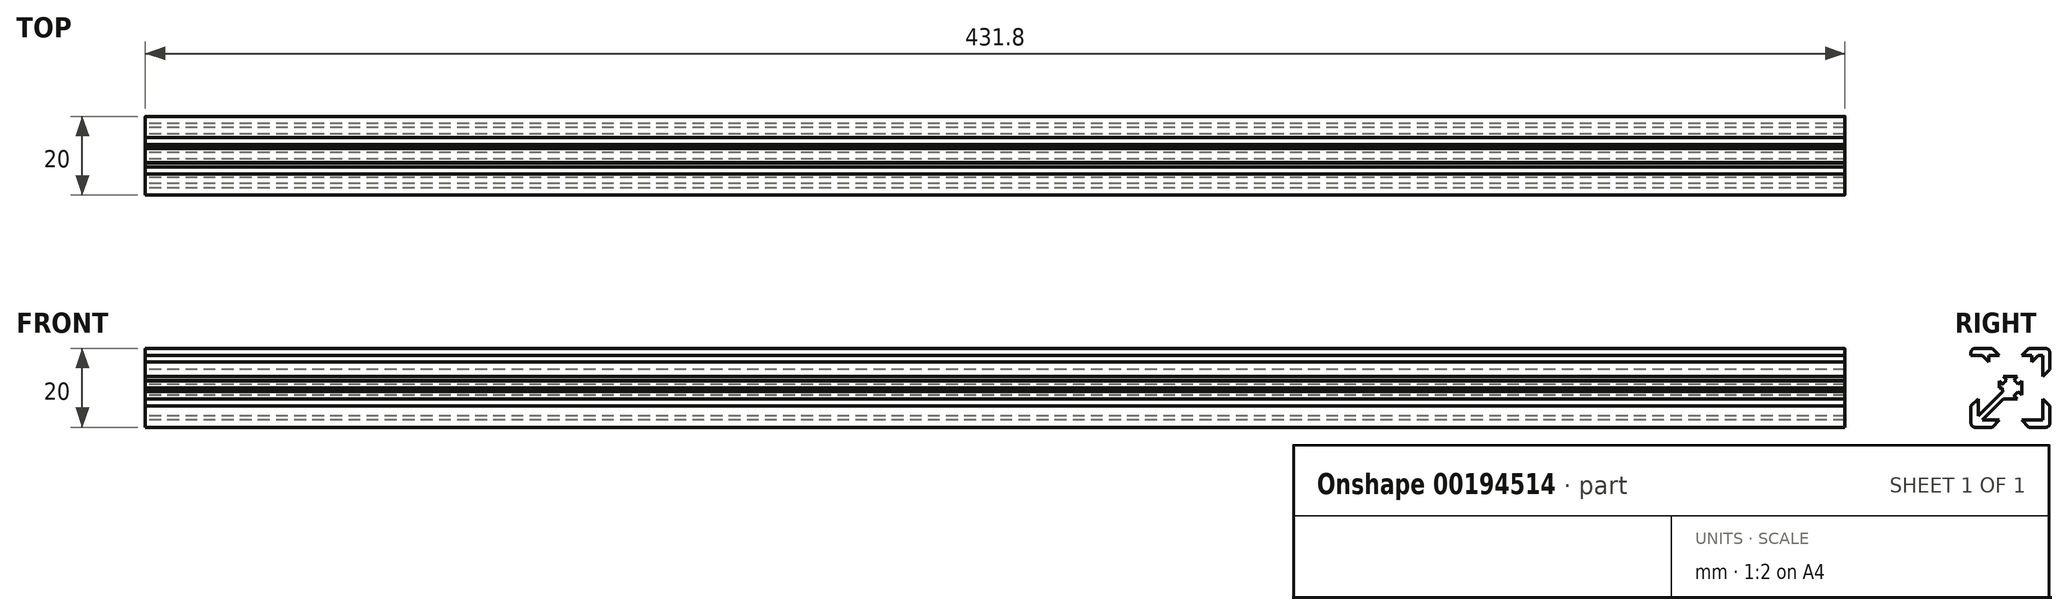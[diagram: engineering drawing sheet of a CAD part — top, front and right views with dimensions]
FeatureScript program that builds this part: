
annotation { "Feature Type Name" : "Feature", "Feature Type Description" : "" }
export const myFeature = defineFeature(function(context is Context, id is Id, definition is map)
    precondition{}
    {
        {
            var Q0;
            Q0=qCreatedBy(makeId("Right.planeOp"),FACE);
            var sketch = newSketch(context, id + "F0", { "sketchPlane" : qUnion([Q0])});
            skArc(sketch, "E0.filletArc", {"start": v(9, -10) * mm, "mid": v(9.7, -9.7) * mm, "end": v(10, -9) * mm});
            skArc(sketch, "E1", {"start": v(2.1, 0) * mm, "mid": v(1.48, -1.48) * mm, "end": v(0, -2.1) * mm});
            skLineSegment(sketch, "E2", {"start": v(0, -2.1) * mm, "end": v(0, -2.84) * mm});
            skLineSegment(sketch, "E3", {"start": v(2.1, 0) * mm, "end": v(2.84, 0) * mm});
            skLineSegment(sketch, "E4", {"start": v(2.84, -8.2) * mm, "end": v(4.64, -10) * mm});
            skLineSegment(sketch, "E5", {"start": v(8.2, -2.84) * mm, "end": v(10, -4.64) * mm});
            skLineSegment(sketch, "E6", {"start": v(4.64, -10) * mm, "end": v(9, -10) * mm});
            skLineSegment(sketch, "E7", {"start": v(10, -4.64) * mm, "end": v(10, -9) * mm});
            skLineSegment(sketch, "E8", {"start": v(2.84, -8.2) * mm, "end": v(10, -8.2) * mm});
            skLineSegment(sketch, "E9", {"start": v(8.2, -2.84) * mm, "end": v(8.2, -10) * mm});
            skLineSegment(sketch, "E10", {"start": v(9, -9) * mm, "end": v(8.2, -8.2) * mm});
            skPoint(sketch, "E11", {"position": v(8.73, -7.67) * mm});
            skPoint(sketch, "E12", {"position": v(7.67, -8.73) * mm});
            skPoint(sketch, "E13", {"position": v(8.2, -8.2) * mm});
            skPoint(sketch, "E14", {"position": v(5.53, -4.47) * mm});
            skPoint(sketch, "E15", {"position": v(4.47, -5.53) * mm});
            skLineSegment(sketch, "E16", {"start": v(7.67, -8.73) * mm, "end": v(4.47, -5.53) * mm});
            skLineSegment(sketch, "E17", {"start": v(8.73, -7.67) * mm, "end": v(5.53, -4.47) * mm});
            skLineSegment(sketch, "E18", {"start": v(5.53, -4.47) * mm, "end": v(1.92, -0.86) * mm});
            skLineSegment(sketch, "E19", {"start": v(4.47, -5.53) * mm, "end": v(0.86, -1.92) * mm});
            skLineSegment(sketch, "E20", {"start": v(8.2, -7.14) * mm, "end": v(8.2, -5.5) * mm});
            skLineSegment(sketch, "E21", {"start": v(7.14, -8.2) * mm, "end": v(5.5, -8.2) * mm});
            skLineSegment(sketch, "E22", {"start": v(5.5, -8.2) * mm, "end": v(5.5, -6.56) * mm});
            skLineSegment(sketch, "E23", {"start": v(8.2, -5.5) * mm, "end": v(6.56, -5.5) * mm});
            skLineSegment(sketch, "E24", {"start": v(2.84, 0) * mm, "end": v(2.84, -1.78) * mm});
            skLineSegment(sketch, "E25", {"start": v(0, -2.84) * mm, "end": v(1.78, -2.84) * mm});
            skArc(sketch, "E26.filletArc", {"start": v(10, 9) * mm, "mid": v(9.7, 9.7) * mm, "end": v(9, 10) * mm});
            skArc(sketch, "E27", {"start": v(0, 2.1) * mm, "mid": v(1.48, 1.48) * mm, "end": v(2.1, 0) * mm});
            skLineSegment(sketch, "E28", {"start": v(0, 2.1) * mm, "end": v(0, 2.84) * mm});
            skLineSegment(sketch, "E29", {"start": v(8.2, 2.84) * mm, "end": v(10, 4.64) * mm});
            skLineSegment(sketch, "E30", {"start": v(2.84, 8.2) * mm, "end": v(4.64, 10) * mm});
            skLineSegment(sketch, "E31", {"start": v(10, 4.64) * mm, "end": v(10, 9) * mm});
            skLineSegment(sketch, "E32", {"start": v(4.64, 10) * mm, "end": v(9, 10) * mm});
            skLineSegment(sketch, "E33", {"start": v(8.2, 2.84) * mm, "end": v(8.2, 10) * mm});
            skLineSegment(sketch, "E34", {"start": v(2.84, 8.2) * mm, "end": v(10, 8.2) * mm});
            skLineSegment(sketch, "E35", {"start": v(9, 9) * mm, "end": v(8.2, 8.2) * mm});
            skPoint(sketch, "E36", {"position": v(7.67, 8.73) * mm});
            skPoint(sketch, "E37", {"position": v(8.73, 7.67) * mm});
            skPoint(sketch, "E38", {"position": v(8.2, 8.2) * mm});
            skPoint(sketch, "E39", {"position": v(4.47, 5.53) * mm});
            skPoint(sketch, "E40", {"position": v(5.53, 4.47) * mm});
            skLineSegment(sketch, "E41", {"start": v(8.73, 7.67) * mm, "end": v(5.53, 4.47) * mm});
            skLineSegment(sketch, "E42", {"start": v(7.67, 8.73) * mm, "end": v(4.47, 5.53) * mm});
            skLineSegment(sketch, "E43", {"start": v(4.47, 5.53) * mm, "end": v(0.86, 1.92) * mm});
            skLineSegment(sketch, "E44", {"start": v(5.53, 4.47) * mm, "end": v(1.92, 0.86) * mm});
            skLineSegment(sketch, "E45", {"start": v(7.14, 8.2) * mm, "end": v(5.5, 8.2) * mm});
            skLineSegment(sketch, "E46", {"start": v(8.2, 7.14) * mm, "end": v(8.2, 5.5) * mm});
            skLineSegment(sketch, "E47", {"start": v(8.2, 5.5) * mm, "end": v(6.56, 5.5) * mm});
            skLineSegment(sketch, "E48", {"start": v(5.5, 8.2) * mm, "end": v(5.5, 6.56) * mm});
            skLineSegment(sketch, "E49", {"start": v(0, 2.84) * mm, "end": v(1.78, 2.84) * mm});
            skLineSegment(sketch, "E50", {"start": v(2.84, 0) * mm, "end": v(2.84, 1.78) * mm});
            skArc(sketch, "E51.filletArc", {"start": v(-9, 10) * mm, "mid": v(-9.7, 9.7) * mm, "end": v(-10, 9) * mm});
            skArc(sketch, "E52", {"start": v(-2.1, 0) * mm, "mid": v(-1.48, 1.48) * mm, "end": v(0, 2.1) * mm});
            skLineSegment(sketch, "E53", {"start": v(-2.1, 0) * mm, "end": v(-2.84, 0) * mm});
            skLineSegment(sketch, "E54", {"start": v(-2.84, 8.2) * mm, "end": v(-4.64, 10) * mm});
            skLineSegment(sketch, "E55", {"start": v(-8.2, 2.84) * mm, "end": v(-10, 4.64) * mm});
            skLineSegment(sketch, "E56", {"start": v(-4.64, 10) * mm, "end": v(-9, 10) * mm});
            skLineSegment(sketch, "E57", {"start": v(-10, 4.64) * mm, "end": v(-10, 9) * mm});
            skLineSegment(sketch, "E58", {"start": v(-2.84, 8.2) * mm, "end": v(-10, 8.2) * mm});
            skLineSegment(sketch, "E59", {"start": v(-8.2, 2.84) * mm, "end": v(-8.2, 10) * mm});
            skLineSegment(sketch, "E60", {"start": v(-9, 9) * mm, "end": v(-8.2, 8.2) * mm});
            skPoint(sketch, "E61", {"position": v(-8.73, 7.67) * mm});
            skPoint(sketch, "E62", {"position": v(-7.67, 8.73) * mm});
            skPoint(sketch, "E63", {"position": v(-8.2, 8.2) * mm});
            skPoint(sketch, "E64", {"position": v(-5.53, 4.47) * mm});
            skPoint(sketch, "E65", {"position": v(-4.47, 5.53) * mm});
            skLineSegment(sketch, "E66", {"start": v(-7.67, 8.73) * mm, "end": v(-4.47, 5.53) * mm});
            skLineSegment(sketch, "E67", {"start": v(-8.73, 7.67) * mm, "end": v(-5.53, 4.47) * mm});
            skLineSegment(sketch, "E68", {"start": v(-5.53, 4.47) * mm, "end": v(-1.92, 0.86) * mm});
            skLineSegment(sketch, "E69", {"start": v(-4.47, 5.53) * mm, "end": v(-0.86, 1.92) * mm});
            skLineSegment(sketch, "E70", {"start": v(-8.2, 7.14) * mm, "end": v(-8.2, 5.5) * mm});
            skLineSegment(sketch, "E71", {"start": v(-7.14, 8.2) * mm, "end": v(-5.5, 8.2) * mm});
            skLineSegment(sketch, "E72", {"start": v(-5.5, 8.2) * mm, "end": v(-5.5, 6.56) * mm});
            skLineSegment(sketch, "E73", {"start": v(-8.2, 5.5) * mm, "end": v(-6.56, 5.5) * mm});
            skLineSegment(sketch, "E74", {"start": v(-2.84, 0) * mm, "end": v(-2.84, 1.78) * mm});
            skLineSegment(sketch, "E75", {"start": v(0, 2.84) * mm, "end": v(-1.78, 2.84) * mm});
            skArc(sketch, "E76.filletArc", {"start": v(-10, -9) * mm, "mid": v(-9.7, -9.7) * mm, "end": v(-9, -10) * mm});
            skArc(sketch, "E77", {"start": v(0, -2.1) * mm, "mid": v(-1.48, -1.48) * mm, "end": v(-2.1, 0) * mm});
            skLineSegment(sketch, "E78", {"start": v(-8.2, -2.84) * mm, "end": v(-10, -4.64) * mm});
            skLineSegment(sketch, "E79", {"start": v(-2.84, -8.2) * mm, "end": v(-4.64, -10) * mm});
            skLineSegment(sketch, "E80", {"start": v(-10, -4.64) * mm, "end": v(-10, -9) * mm});
            skLineSegment(sketch, "E81", {"start": v(-4.64, -10) * mm, "end": v(-9, -10) * mm});
            skLineSegment(sketch, "E82", {"start": v(-8.2, -2.84) * mm, "end": v(-8.2, -10) * mm});
            skLineSegment(sketch, "E83", {"start": v(-2.84, -8.2) * mm, "end": v(-10, -8.2) * mm});
            skLineSegment(sketch, "E84", {"start": v(-9, -9) * mm, "end": v(-8.2, -8.2) * mm});
            skPoint(sketch, "E85", {"position": v(-7.67, -8.73) * mm});
            skPoint(sketch, "E86", {"position": v(-8.73, -7.67) * mm});
            skPoint(sketch, "E87", {"position": v(-8.2, -8.2) * mm});
            skPoint(sketch, "E88", {"position": v(-4.47, -5.53) * mm});
            skPoint(sketch, "E89", {"position": v(-5.53, -4.47) * mm});
            skLineSegment(sketch, "E90", {"start": v(-8.73, -7.67) * mm, "end": v(-5.53, -4.47) * mm});
            skLineSegment(sketch, "E91", {"start": v(-7.67, -8.73) * mm, "end": v(-4.47, -5.53) * mm});
            skLineSegment(sketch, "E92", {"start": v(-4.47, -5.53) * mm, "end": v(-0.86, -1.92) * mm});
            skLineSegment(sketch, "E93", {"start": v(-5.53, -4.47) * mm, "end": v(-1.92, -0.86) * mm});
            skLineSegment(sketch, "E94", {"start": v(-7.14, -8.2) * mm, "end": v(-5.5, -8.2) * mm});
            skLineSegment(sketch, "E95", {"start": v(-8.2, -7.14) * mm, "end": v(-8.2, -5.5) * mm});
            skLineSegment(sketch, "E96", {"start": v(-8.2, -5.5) * mm, "end": v(-6.56, -5.5) * mm});
            skLineSegment(sketch, "E97", {"start": v(-5.5, -8.2) * mm, "end": v(-5.5, -6.56) * mm});
            skLineSegment(sketch, "E98", {"start": v(0, -2.84) * mm, "end": v(-1.78, -2.84) * mm});
            skLineSegment(sketch, "E99", {"start": v(-2.84, 0) * mm, "end": v(-2.84, -1.78) * mm});
            skLineSegment(sketch, "E100", {"start": v(-1.78, -2.84) * mm, "end": v(-2.84, -1.78) * mm});
            skLineSegment(sketch, "E101", {"start": v(-10, 8.2) * mm, "end": v(-10, 9) * mm});
            skLineSegment(sketch, "E102", {"start": v(-9, 10) * mm, "end": v(-4.64, 10) * mm});
            skLineSegment(sketch, "E103", {"start": v(-2.84, 8.2) * mm, "end": v(-7.14, 8.2) * mm});
            skLineSegment(sketch, "E104", {"start": v(-1.78, 2.84) * mm, "end": v(1.78, 2.84) * mm});
            skLineSegment(sketch, "E105", {"start": v(7.14, 8.2) * mm, "end": v(2.84, 8.2) * mm});
            skLineSegment(sketch, "E106", {"start": v(10, 9) * mm, "end": v(10, 4.64) * mm});
            skLineSegment(sketch, "E107", {"start": v(8.2, 2.84) * mm, "end": v(8.2, 5.5) * mm});
            skSolve(sketch);
        }
        {
            var Q0;
            {var subQ5=sQuery(id+"F0.wireOp",EDGE,"E0.filletArc");Q0=makeQuery(id+"F0.imprint","IMPRINT",FACE,{"disambiguationData":[TD([[makeQuery(id+"F0.imprint","IMPRINT",EDGE,{"derivedFrom":subQ5}),1.0]])]});}
            var Q1;
            {var subQ0=sQuery(id+"F0.wireOp",EDGE,"E21");Q1=makeQuery(id+"F0.imprint","IMPRINT",FACE,{"disambiguationData":[TD([[makeQuery(id+"F0.imprint","IMPRINT",EDGE,{"derivedFrom":subQ0}),-1.0]])]});}
            var Q2;
            {var subQ0=sQuery(id+"F0.wireOp",EDGE,"E20");Q2=makeQuery(id+"F0.imprint","IMPRINT",FACE,{"disambiguationData":[TD([[makeQuery(id+"F0.imprint","IMPRINT",EDGE,{"derivedFrom":subQ0}),1.0]])]});}
            var Q3;
            {var subQ6=sQuery(id+"F0.wireOp",EDGE,"E26.filletArc");Q3=makeQuery(id+"F0.imprint","IMPRINT",FACE,{"disambiguationData":[TD([[makeQuery(id+"F0.imprint","IMPRINT",EDGE,{"derivedFrom":subQ6}),1.0]])]});}
            var Q4;
            {var subQ0=sQuery(id+"F0.wireOp",EDGE,"E46");Q4=makeQuery(id+"F0.imprint","IMPRINT",FACE,{"disambiguationData":[TD([[makeQuery(id+"F0.imprint","IMPRINT",EDGE,{"derivedFrom":subQ0}),-1.0]])]});}
            var Q5;
            {var subQ3=sQuery(id+"F0.wireOp",EDGE,"E48");Q5=makeQuery(id+"F0.imprint","IMPRINT",FACE,{"disambiguationData":[TD([[makeQuery(id+"F0.imprint","IMPRINT",EDGE,{"derivedFrom":subQ3}),1.0]])]});}
            var Q6;
            {var subQ6=sQuery(id+"F0.wireOp",EDGE,"E51.filletArc");Q6=makeQuery(id+"F0.imprint","IMPRINT",FACE,{"disambiguationData":[TD([[makeQuery(id+"F0.imprint","IMPRINT",EDGE,{"derivedFrom":subQ6}),1.0]])]});}
            var Q7;
            {var subQ3=sQuery(id+"F0.wireOp",EDGE,"E72");Q7=makeQuery(id+"F0.imprint","IMPRINT",FACE,{"disambiguationData":[TD([[makeQuery(id+"F0.imprint","IMPRINT",EDGE,{"derivedFrom":subQ3}),-1.0]])]});}
            var Q8;
            {var subQ0=sQuery(id+"F0.wireOp",EDGE,"E70");Q8=makeQuery(id+"F0.imprint","IMPRINT",FACE,{"disambiguationData":[TD([[makeQuery(id+"F0.imprint","IMPRINT",EDGE,{"derivedFrom":subQ0}),1.0]])]});}
            var Q9;
            {var subQ5=sQuery(id+"F0.wireOp",EDGE,"E76.filletArc");Q9=makeQuery(id+"F0.imprint","IMPRINT",FACE,{"disambiguationData":[TD([[makeQuery(id+"F0.imprint","IMPRINT",EDGE,{"derivedFrom":subQ5}),1.0]])]});}
            var Q10;
            {var subQ0=sQuery(id+"F0.wireOp",EDGE,"E95");Q10=makeQuery(id+"F0.imprint","IMPRINT",FACE,{"disambiguationData":[TD([[makeQuery(id+"F0.imprint","IMPRINT",EDGE,{"derivedFrom":subQ0}),-1.0]])]});}
            var Q11;
            {var subQ0=sQuery(id+"F0.wireOp",EDGE,"E94");Q11=makeQuery(id+"F0.imprint","IMPRINT",FACE,{"disambiguationData":[TD([[makeQuery(id+"F0.imprint","IMPRINT",EDGE,{"derivedFrom":subQ0}),1.0]])]});}
            var Q12;
            {var subQ4=sQuery(id+"F0.wireOp",EDGE,"E24");Q12=makeQuery(id+"F0.imprint","IMPRINT",FACE,{"disambiguationData":[TD([[makeQuery(id+"F0.imprint","IMPRINT",EDGE,{"derivedFrom":subQ4}),-1.0]])]});}
            var Q13;
            {var subQ4=sQuery(id+"F0.wireOp",EDGE,"E25");Q13=makeQuery(id+"F0.imprint","IMPRINT",FACE,{"disambiguationData":[TD([[makeQuery(id+"F0.imprint","IMPRINT",EDGE,{"derivedFrom":subQ4}),1.0]])]});}
            var Q14;
            {var subQ0=sQuery(id+"F0.wireOp",EDGE,"E2");Q14=makeQuery(id+"F0.imprint","IMPRINT",FACE,{"disambiguationData":[TD([[makeQuery(id+"F0.imprint","IMPRINT",EDGE,{"derivedFrom":subQ0}),1.0]])]});}
            var Q15;
            {var subQ0=sQuery(id+"F0.wireOp",EDGE,"E2");Q15=makeQuery(id+"F0.imprint","IMPRINT",FACE,{"disambiguationData":[TD([[makeQuery(id+"F0.imprint","IMPRINT",EDGE,{"derivedFrom":subQ0}),-1.0]])]});}
            var Q16;
            {var subQ4=sQuery(id+"F0.wireOp",EDGE,"E4");Q16=makeQuery(id+"F0.imprint","IMPRINT",FACE,{"disambiguationData":[TD([[makeQuery(id+"F0.imprint","IMPRINT",EDGE,{"derivedFrom":subQ4}),1.0]])]});}
            var Q17;
            {var subQ1=sQuery(id+"F0.wireOp",EDGE,"E5");Q17=makeQuery(id+"F0.imprint","IMPRINT",FACE,{"disambiguationData":[TD([[makeQuery(id+"F0.imprint","IMPRINT",EDGE,{"derivedFrom":subQ1}),-1.0]])]});}
            var Q18;
            {var subQ0=sQuery(id+"F0.wireOp",EDGE,"E28");Q18=makeQuery(id+"F0.imprint","IMPRINT",FACE,{"disambiguationData":[TD([[makeQuery(id+"F0.imprint","IMPRINT",EDGE,{"derivedFrom":subQ0}),-1.0]])]});}
            var Q19;
            {var subQ0=sQuery(id+"F0.wireOp",EDGE,"E3");Q19=makeQuery(id+"F0.imprint","IMPRINT",FACE,{"disambiguationData":[TD([[makeQuery(id+"F0.imprint","IMPRINT",EDGE,{"derivedFrom":subQ0}),1.0]])]});}
            var Q20;
            {var subQ0=sQuery(id+"F0.wireOp",EDGE,"E28");Q20=makeQuery(id+"F0.imprint","IMPRINT",FACE,{"disambiguationData":[TD([[makeQuery(id+"F0.imprint","IMPRINT",EDGE,{"derivedFrom":subQ0}),1.0]])]});}
            var Q21;
            {var subQ0=sQuery(id+"F0.wireOp",EDGE,"E28");Q21=makeQuery(id+"F0.imprint","IMPRINT",FACE,{"disambiguationData":[TD([[makeQuery(id+"F0.imprint","IMPRINT",EDGE,{"derivedFrom":subQ0}),-1.0]])]});}
            var Q22;
            {var subQ5=sQuery(id+"F0.wireOp",EDGE,"E29");Q22=makeQuery(id+"F0.imprint","IMPRINT",FACE,{"disambiguationData":[TD([[makeQuery(id+"F0.imprint","IMPRINT",EDGE,{"derivedFrom":subQ5}),1.0]])]});}
            var Q23;
            {var subQ4=sQuery(id+"F0.wireOp",EDGE,"E30");Q23=makeQuery(id+"F0.imprint","IMPRINT",FACE,{"disambiguationData":[TD([[makeQuery(id+"F0.imprint","IMPRINT",EDGE,{"derivedFrom":subQ4}),-1.0]])]});}
            var Q24;
            {var subQ4=sQuery(id+"F0.wireOp",EDGE,"E74");Q24=makeQuery(id+"F0.imprint","IMPRINT",FACE,{"disambiguationData":[TD([[makeQuery(id+"F0.imprint","IMPRINT",EDGE,{"derivedFrom":subQ4}),-1.0]])]});}
            var Q25;
            {var subQ1=sQuery(id+"F0.wireOp",EDGE,"E54");Q25=makeQuery(id+"F0.imprint","IMPRINT",FACE,{"disambiguationData":[TD([[makeQuery(id+"F0.imprint","IMPRINT",EDGE,{"derivedFrom":subQ1}),1.0]])]});}
            var Q26;
            {var subQ5=sQuery(id+"F0.wireOp",EDGE,"E57");Q26=makeQuery(id+"F0.imprint","IMPRINT",FACE,{"disambiguationData":[TD([[makeQuery(id+"F0.imprint","IMPRINT",EDGE,{"derivedFrom":subQ5}),-1.0]])]});}
            var Q27;
            {var subQ0=sQuery(id+"F0.wireOp",EDGE,"E53");Q27=makeQuery(id+"F0.imprint","IMPRINT",FACE,{"disambiguationData":[TD([[makeQuery(id+"F0.imprint","IMPRINT",EDGE,{"derivedFrom":subQ0}),1.0]])]});}
            var Q28;
            {var subQ4=sQuery(id+"F0.wireOp",EDGE,"E78");Q28=makeQuery(id+"F0.imprint","IMPRINT",FACE,{"disambiguationData":[TD([[makeQuery(id+"F0.imprint","IMPRINT",EDGE,{"derivedFrom":subQ4}),1.0]])]});}
            var Q29;
            {var subQ1=sQuery(id+"F0.wireOp",EDGE,"E79");Q29=makeQuery(id+"F0.imprint","IMPRINT",FACE,{"disambiguationData":[TD([[makeQuery(id+"F0.imprint","IMPRINT",EDGE,{"derivedFrom":subQ1}),-1.0]])]});}
            var Q30;
            {var subQ5=sQuery(id+"F0.wireOp",EDGE,"E100");Q30=makeQuery(id+"F0.imprint","IMPRINT",FACE,{"disambiguationData":[TD([[makeQuery(id+"F0.imprint","IMPRINT",EDGE,{"derivedFrom":subQ5}),-1.0]])]});}
            var Q31;
            {var subQ6=sQuery(id+"F0.wireOp",EDGE,"E100");Q31=makeQuery(id+"F0.imprint","IMPRINT",FACE,{"disambiguationData":[TD([[makeQuery(id+"F0.imprint","IMPRINT",EDGE,{"derivedFrom":subQ6}),1.0]])]});}
            var Q32;
            {var subQ0=sQuery(id+"F0.wireOp",EDGE,"E18");var subQ15=sQuery(id+"F0.wireOp",EDGE,"E1");var subQ16=makeQuery(id+"F0.imprint","INTERSECT",VERTEX,{"derivedFrom":[subQ15,subQ0]});Q32=makeQuery(id+"F0.imprint","IMPRINT",FACE,{"disambiguationData":[TD([[makeQuery(id+"F0.imprint","IMPRINT",EDGE,{"disambiguationData":[TD([[subQ16,-1.0]])],"derivedFrom":subQ15}),1.0]])]});}
            var Q33;
            {var subQ4=sQuery(id+"F0.wireOp",EDGE,"E43");var subQ5=sQuery(id+"F0.wireOp",EDGE,"E27");var subQ6=makeQuery(id+"F0.imprint","INTERSECT",VERTEX,{"derivedFrom":[subQ5,subQ4]});Q33=makeQuery(id+"F0.imprint","IMPRINT",FACE,{"disambiguationData":[TD([[makeQuery(id+"F0.imprint","IMPRINT",EDGE,{"disambiguationData":[TD([[subQ6,-1.0]])],"derivedFrom":subQ5}),1.0]])]});}
            var Q34;
            {var subQ0=sQuery(id+"F0.wireOp",EDGE,"E68");var subQ9=sQuery(id+"F0.wireOp",EDGE,"E52");var subQ10=makeQuery(id+"F0.imprint","INTERSECT",VERTEX,{"derivedFrom":[subQ9,subQ0]});Q34=makeQuery(id+"F0.imprint","IMPRINT",FACE,{"disambiguationData":[TD([[makeQuery(id+"F0.imprint","IMPRINT",EDGE,{"disambiguationData":[TD([[subQ10,-1.0]])],"derivedFrom":subQ9}),1.0]])]});}
            var Q35;
            Q35=sQuery(id+"F0.wireOp",EDGE,"E1");
            var Q36;
            Q36=sQuery(id+"F0.wireOp",EDGE,"E77");
            var Q37;
            Q37=sQuery(id+"F0.wireOp",EDGE,"E52");
            var Q38;
            Q38=sQuery(id+"F0.wireOp",EDGE,"E27");
            var Q39;
            Q39=sQuery(id+"F0.wireOp",EDGE,"E44");
            var Q40;
            Q40=sQuery(id+"F0.wireOp",EDGE,"E41");
            var Q41;
            Q41=sQuery(id+"F0.wireOp",EDGE,"E47");
            var Q42;
            Q42=sQuery(id+"F0.wireOp",EDGE,"E107");
            var Q43;
            Q43=sQuery(id+"F0.wireOp",EDGE,"E29");
            var Q44;
            Q44=sQuery(id+"F0.wireOp",EDGE,"E106");
            var Q45;
            Q45=sQuery(id+"F0.wireOp",EDGE,"E26.filletArc");
            var Q46;
            Q46=sQuery(id+"F0.wireOp",EDGE,"E32");
            var Q47;
            Q47=sQuery(id+"F0.wireOp",EDGE,"E30");
            var Q48;
            Q48=sQuery(id+"F0.wireOp",EDGE,"E34");
            var Q49;
            Q49=sQuery(id+"F0.wireOp",EDGE,"E48");
            var Q50;
            Q50=sQuery(id+"F0.wireOp",EDGE,"E42");
            var Q51;
            Q51=sQuery(id+"F0.wireOp",EDGE,"E43");
            var Q52;
            Q52=sQuery(id+"F0.wireOp",EDGE,"E104");
            var Q53;
            Q53=sQuery(id+"F0.wireOp",EDGE,"E69");
            var Q54;
            Q54=sQuery(id+"F0.wireOp",EDGE,"E66");
            var Q55;
            Q55=sQuery(id+"F0.wireOp",EDGE,"E72");
            var Q56;
            Q56=sQuery(id+"F0.wireOp",EDGE,"E58");
            var Q57;
            Q57=sQuery(id+"F0.wireOp",EDGE,"E54");
            var Q58;
            Q58=sQuery(id+"F0.wireOp",EDGE,"E56");
            var Q59;
            Q59=sQuery(id+"F0.wireOp",EDGE,"E51.filletArc");
            var Q60;
            Q60=sQuery(id+"F0.wireOp",EDGE,"E57");
            var Q61;
            Q61=sQuery(id+"F0.wireOp",EDGE,"E55");
            extrude(context, id + "F1", {"entities" : qUnion([Q0, Q1, Q2, Q3, Q4, Q5, Q6, Q7, Q8, Q9, Q10, Q11, Q12, Q13, Q14, Q15, Q16, Q17, Q18, Q19, Q20, Q21, Q22, Q23, Q24, Q25, Q26, Q27, Q28, Q29, Q30, Q31, Q32, Q33, Q34]), "surfaceEntities" : qUnion([Q35, Q36, Q37, Q38, Q39, Q40, Q41, Q42, Q43, Q44, Q45, Q46, Q47, Q48, Q49, Q50, Q51, Q52, Q53, Q54, Q55, Q56, Q57, Q58, Q59, Q60, Q61]), "depth" : 431.8 * mm, "offsetDistance" : 25.4 * mm});
        }
    });
